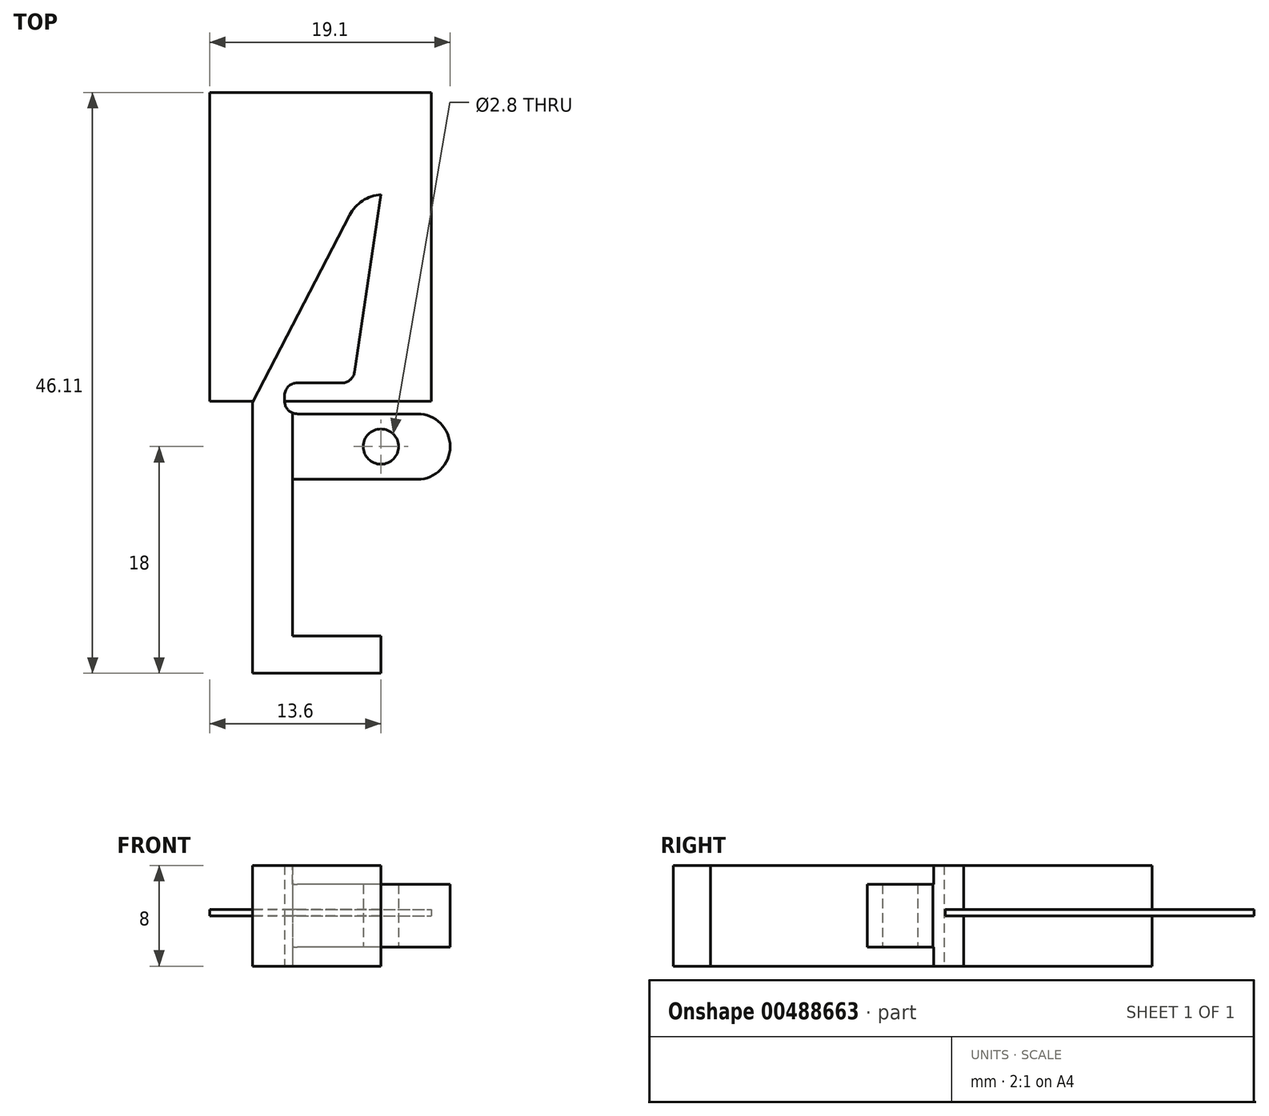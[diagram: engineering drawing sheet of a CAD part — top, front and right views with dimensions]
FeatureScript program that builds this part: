
annotation { "Feature Type Name" : "Feature", "Feature Type Description" : "" }
export const myFeature = defineFeature(function(context is Context, id is Id, definition is map)
    precondition{}
    {
        {
            var Q0;
            Q0=qCreatedBy(makeId("Top.planeOp"),FACE);
            var sketch = newSketch(context, id + "F0", { "sketchPlane" : qUnion([Q0])});
            skLineSegment(sketch, "E0.bottom", {"start": v(0, 0) * mm, "end": v(-10.2, 0) * mm});
            skLineSegment(sketch, "E0.top", {"start": v(0, 2.95) * mm, "end": v(-7, 2.95) * mm});
            skLineSegment(sketch, "E0.left", {"start": v(0, 0) * mm, "end": v(0, 2.95) * mm});
            skLineSegment(sketch, "E0.right", {"start": v(-10.2, 0) * mm, "end": v(-10.2, 2.95) * mm});
            skLineSegment(sketch, "E1.left", {"start": v(-10.2, 2.95) * mm, "end": v(-10.2, 21.5) * mm});
            skArc(sketch, "E2", {"start": v(2.9, 15.4) * mm, "mid": v(5.5, 18) * mm, "end": v(2.9, 20.6) * mm});
            skLineSegment(sketch, "E3", {"start": v(2.9, 20.6) * mm, "end": v(-6.64, 20.6) * mm});
            skLineSegment(sketch, "E4", {"start": v(2.9, 15.4) * mm, "end": v(-7, 15.4) * mm});
            skCircle(sketch, "E5", {"center": v(0, 18) * mm, "radius": 1.4 * mm});
            skLineSegment(sketch, "E6", {"start": v(0, 18) * mm, "end": v(0, 39.6) * mm, "construction": true});
            skLineSegment(sketch, "E7", {"start": v(-7, 15.4) * mm, "end": v(-7, 2.95) * mm});
            skLineSegment(sketch, "E8", {"start": v(-2.47, 36.39) * mm, "end": v(-10.2, 21.5) * mm});
            skPoint(sketch, "E9.visualSharp", {"position": v(-1.65, 37.97) * mm});
            skArc(sketch, "E9.filletArc", {"start": v(0, 38) * mm, "mid": v(-1.45, 37.52) * mm, "end": v(-2.47, 36.39) * mm});
            skLineSegment(sketch, "E10", {"start": v(-7.64, 21.6) * mm, "end": v(-7.64, 22.06) * mm});
            skLineSegment(sketch, "E11", {"start": v(-6.64, 23.06) * mm, "end": v(-3.08, 23.06) * mm});
            skLineSegment(sketch, "E12", {"start": v(-2.1, 23.91) * mm, "end": v(0, 38) * mm});
            skPoint(sketch, "E13.visualSharp", {"position": v(-7.64, 20.6) * mm});
            skArc(sketch, "E13.filletArc", {"start": v(-7.64, 21.6) * mm, "mid": v(-7.35, 20.9) * mm, "end": v(-6.64, 20.6) * mm});
            skPoint(sketch, "E14.visualSharp", {"position": v(-7.64, 23.06) * mm});
            skArc(sketch, "E14.filletArc", {"start": v(-6.64, 23.06) * mm, "mid": v(-7.35, 22.76) * mm, "end": v(-7.64, 22.06) * mm});
            skPoint(sketch, "E15.visualSharp", {"position": v(-2.22, 23.06) * mm});
            skArc(sketch, "E15.filletArc", {"start": v(-3.08, 23.06) * mm, "mid": v(-2.43, 23.3) * mm, "end": v(-2.1, 23.91) * mm});
            skPoint(sketch, "E16.orphan", {"position": v(5.5, 18) * mm});
            skSolve(sketch);
        }
        {
            var Q0;
            Q0=makeQuery(id+"F0.imprint","IMPRINT",FACE,{"disambiguationData":[TD([[makeQuery(id+"F0.imprint","IMPRINT",EDGE,{"derivedFrom":sQuery(id+"F0.wireOp",EDGE,"E0.bottom")}),-1.0]])]});
            extrude(context, id + "F1", {"entities" : qUnion([Q0]), "depth" : 8 * mm});
        }
        {
            var Q0;
            Q0=makeQuery(id+"F1.opExtrude","CAP_FACE",FACE,{"disambiguationData":[OSD([sQuery(id+"F0.wireOp",EDGE,"E0.bottom"),sQuery(id+"F0.wireOp",EDGE,"E0.top"),sQuery(id+"F0.wireOp",EDGE,"E0.left"),sQuery(id+"F0.wireOp",EDGE,"E0.right"),sQuery(id+"F0.wireOp",EDGE,"E1.left"),sQuery(id+"F0.wireOp",EDGE,"E2"),sQuery(id+"F0.wireOp",EDGE,"E3"),sQuery(id+"F0.wireOp",EDGE,"E4"),sQuery(id+"F0.wireOp",EDGE,"E5"),sQuery(id+"F0.wireOp",EDGE,"E7"),sQuery(id+"F0.wireOp",EDGE,"E8"),sQuery(id+"F0.wireOp",EDGE,"E9.filletArc"),sQuery(id+"F0.wireOp",EDGE,"E10"),sQuery(id+"F0.wireOp",EDGE,"E11"),sQuery(id+"F0.wireOp",EDGE,"E12"),sQuery(id+"F0.wireOp",EDGE,"E13.filletArc"),sQuery(id+"F0.wireOp",EDGE,"E14.filletArc"),sQuery(id+"F0.wireOp",EDGE,"E15.filletArc")])],"isStart":false});
            var Q1;
            Q1=makeQuery(id+"F1.opExtrude","CAP_FACE",FACE,{"disambiguationData":[OSD([sQuery(id+"F0.wireOp",EDGE,"E0.bottom"),sQuery(id+"F0.wireOp",EDGE,"E0.top"),sQuery(id+"F0.wireOp",EDGE,"E0.left"),sQuery(id+"F0.wireOp",EDGE,"E0.right"),sQuery(id+"F0.wireOp",EDGE,"E1.left"),sQuery(id+"F0.wireOp",EDGE,"E2"),sQuery(id+"F0.wireOp",EDGE,"E3"),sQuery(id+"F0.wireOp",EDGE,"E4"),sQuery(id+"F0.wireOp",EDGE,"E5"),sQuery(id+"F0.wireOp",EDGE,"E7"),sQuery(id+"F0.wireOp",EDGE,"E8"),sQuery(id+"F0.wireOp",EDGE,"E9.filletArc"),sQuery(id+"F0.wireOp",EDGE,"E10"),sQuery(id+"F0.wireOp",EDGE,"E11"),sQuery(id+"F0.wireOp",EDGE,"E12"),sQuery(id+"F0.wireOp",EDGE,"E13.filletArc"),sQuery(id+"F0.wireOp",EDGE,"E14.filletArc"),sQuery(id+"F0.wireOp",EDGE,"E15.filletArc")])],"isStart":true});
            cPlane(context, id + "F2", {"entities" : qUnion([Q0, Q1]), "cplaneType" : CPlaneType.MID_PLANE, "offset" : 25 * mm, "width" : 150 * mm, "height" : 150 * mm});
        }
        {
            var Q0;
            Q0=qCreatedBy(id+"F2.planeOp",FACE);
            var sketch = newSketch(context, id + "F3", { "sketchPlane" : qUnion([Q0])});
            skLineSegment(sketch, "E17.bottom", {"start": v(-13.6, 21.6) * mm, "end": v(3.99, 21.6) * mm});
            skLineSegment(sketch, "E17.top", {"start": v(-13.6, 46.11) * mm, "end": v(3.99, 46.11) * mm});
            skLineSegment(sketch, "E17.left", {"start": v(-13.6, 21.6) * mm, "end": v(-13.6, 46.11) * mm});
            skLineSegment(sketch, "E17.right", {"start": v(3.99, 21.6) * mm, "end": v(3.99, 46.11) * mm});
            skSolve(sketch);
        }
        {
            var Q0;
            Q0=makeQuery(id+"F3.imprint","IMPRINT",FACE,{"disambiguationData":[TD([[makeQuery(id+"F3.imprint","IMPRINT",EDGE,{"derivedFrom":sQuery(id+"F3.wireOp",EDGE,"E17.bottom")}),1.0]])]});
            extrude(context, id + "F4", {"entities" : qUnion([Q0]), "operationType" : NewBodyOperationType.ADD, "depth" : 0.5 * mm});
        }
        {
            var Q0;
            Q0=makeQuery(id+"F1.opExtrude","CAP_FACE",FACE,{"disambiguationData":[OSD([sQuery(id+"F0.wireOp",EDGE,"E0.bottom"),sQuery(id+"F0.wireOp",EDGE,"E0.top"),sQuery(id+"F0.wireOp",EDGE,"E0.left"),sQuery(id+"F0.wireOp",EDGE,"E0.right"),sQuery(id+"F0.wireOp",EDGE,"E1.left"),sQuery(id+"F0.wireOp",EDGE,"E2"),sQuery(id+"F0.wireOp",EDGE,"E3"),sQuery(id+"F0.wireOp",EDGE,"E4"),sQuery(id+"F0.wireOp",EDGE,"E5"),sQuery(id+"F0.wireOp",EDGE,"E7"),sQuery(id+"F0.wireOp",EDGE,"E8"),sQuery(id+"F0.wireOp",EDGE,"E9.filletArc"),sQuery(id+"F0.wireOp",EDGE,"E10"),sQuery(id+"F0.wireOp",EDGE,"E11"),sQuery(id+"F0.wireOp",EDGE,"E12"),sQuery(id+"F0.wireOp",EDGE,"E13.filletArc"),sQuery(id+"F0.wireOp",EDGE,"E14.filletArc"),sQuery(id+"F0.wireOp",EDGE,"E15.filletArc")])],"isStart":false});
            var sketch = newSketch(context, id + "F5", { "sketchPlane" : qUnion([Q0])});
            skLineSegment(sketch, "E18.bottom", {"start": v(-7, 15.4) * mm, "end": v(7.59, 15.4) * mm});
            skLineSegment(sketch, "E18.top", {"start": v(-7, 21.2) * mm, "end": v(7.59, 21.2) * mm});
            skLineSegment(sketch, "E18.left", {"start": v(-7, 15.4) * mm, "end": v(-7, 21.2) * mm});
            skLineSegment(sketch, "E18.right", {"start": v(7.59, 15.4) * mm, "end": v(7.59, 21.2) * mm});
            skSolve(sketch);
        }
        {
            var Q0;
            {var subQ2=makeQuery(id+"F1.opExtrude","CAP_EDGE",EDGE,{"disambiguationData":[OSD([sQuery(id+"F0.wireOp",EDGE,"E2")])],"isStart":false});Q0=makeQuery(id+"F5.imprint","IMPRINT",FACE,{"disambiguationData":[TD([[makeQuery(id+"F5.imprint","IMPRINT",EDGE,{"derivedFrom":subQ2}),1.0]])]});}
            extrude(context, id + "F6", {"entities" : qUnion([Q0]), "operationType" : NewBodyOperationType.REMOVE, "oppositeDirection" : true, "depth" : 1.5 * mm});
        }
        {
            var Q0;
            Q0=makeQuery(id+"F1.opExtrude","CAP_FACE",FACE,{"disambiguationData":[OSD([sQuery(id+"F0.wireOp",EDGE,"E0.bottom"),sQuery(id+"F0.wireOp",EDGE,"E0.top"),sQuery(id+"F0.wireOp",EDGE,"E0.left"),sQuery(id+"F0.wireOp",EDGE,"E0.right"),sQuery(id+"F0.wireOp",EDGE,"E1.left"),sQuery(id+"F0.wireOp",EDGE,"E2"),sQuery(id+"F0.wireOp",EDGE,"E3"),sQuery(id+"F0.wireOp",EDGE,"E4"),sQuery(id+"F0.wireOp",EDGE,"E5"),sQuery(id+"F0.wireOp",EDGE,"E7"),sQuery(id+"F0.wireOp",EDGE,"E8"),sQuery(id+"F0.wireOp",EDGE,"E9.filletArc"),sQuery(id+"F0.wireOp",EDGE,"E10"),sQuery(id+"F0.wireOp",EDGE,"E11"),sQuery(id+"F0.wireOp",EDGE,"E12"),sQuery(id+"F0.wireOp",EDGE,"E13.filletArc"),sQuery(id+"F0.wireOp",EDGE,"E14.filletArc"),sQuery(id+"F0.wireOp",EDGE,"E15.filletArc")])],"isStart":true});
            var sketch = newSketch(context, id + "F7", { "sketchPlane" : qUnion([Q0])});
            skLineSegment(sketch, "E19.bottom", {"start": v(-7, -15.4) * mm, "end": v(6.58, -15.4) * mm});
            skLineSegment(sketch, "E19.top", {"start": v(-7, -21.24) * mm, "end": v(6.58, -21.24) * mm});
            skLineSegment(sketch, "E19.left", {"start": v(-7, -15.4) * mm, "end": v(-7, -21.24) * mm});
            skLineSegment(sketch, "E19.right", {"start": v(6.58, -15.4) * mm, "end": v(6.58, -21.24) * mm});
            skSolve(sketch);
        }
        {
            var Q0;
            {var subQ2=makeQuery(id+"F1.opExtrude","CAP_EDGE",EDGE,{"disambiguationData":[OSD([sQuery(id+"F0.wireOp",EDGE,"E2")])],"isStart":true});Q0=makeQuery(id+"F7.imprint","IMPRINT",FACE,{"disambiguationData":[TD([[makeQuery(id+"F7.imprint","IMPRINT",EDGE,{"derivedFrom":subQ2}),-1.0]])]});}
            extrude(context, id + "F8", {"entities" : qUnion([Q0]), "operationType" : NewBodyOperationType.REMOVE, "oppositeDirection" : true, "depth" : 1.5 * mm});
        }
    });
